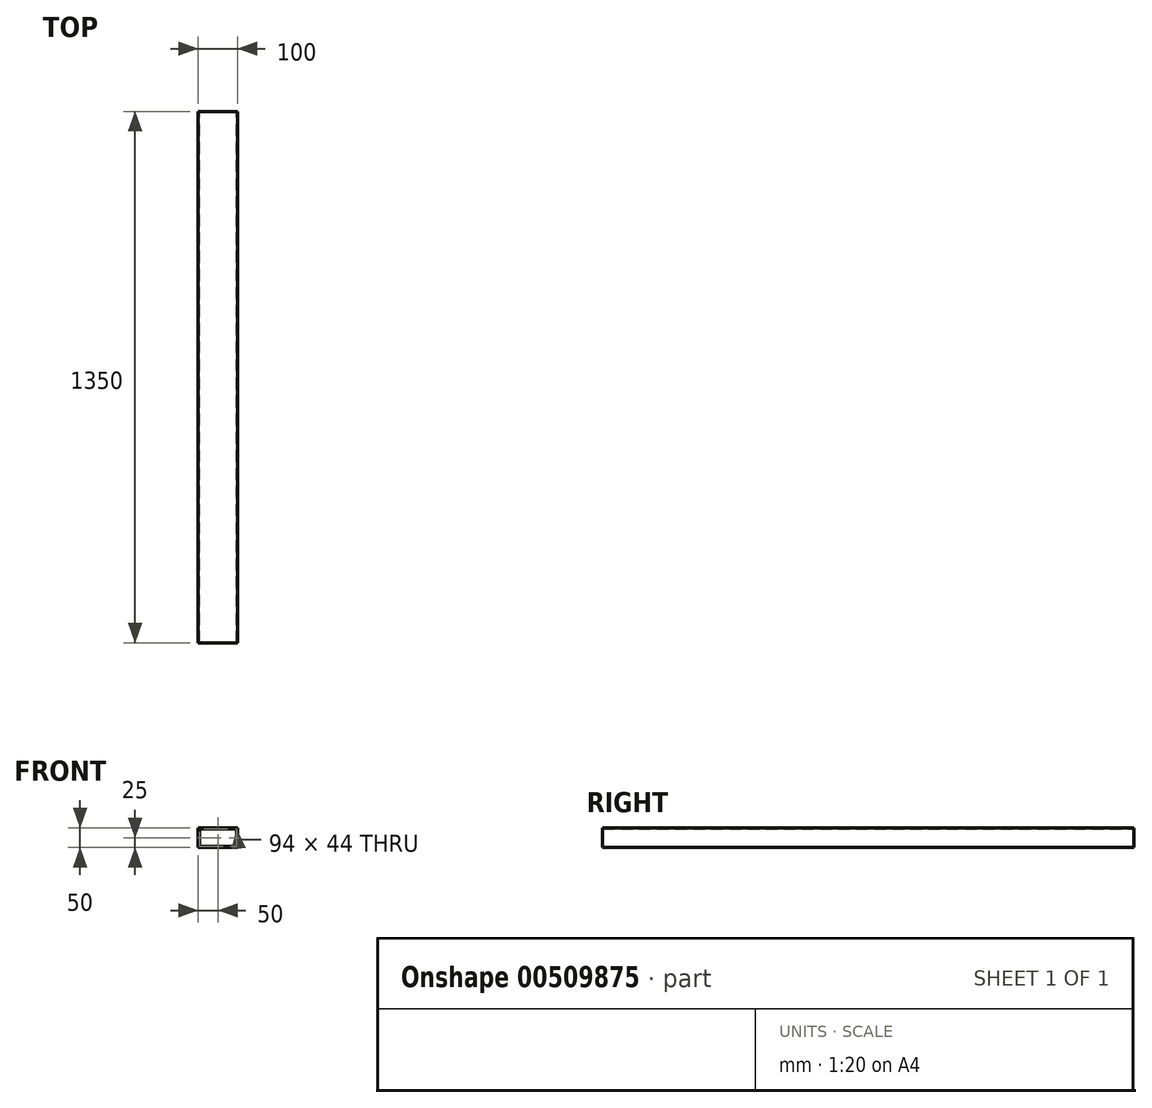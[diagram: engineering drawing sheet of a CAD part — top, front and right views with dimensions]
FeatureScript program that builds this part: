
annotation { "Feature Type Name" : "Feature", "Feature Type Description" : "" }
export const myFeature = defineFeature(function(context is Context, id is Id, definition is map)
    precondition{}
    {
        {
            var Q0;
            Q0=qCreatedBy(makeId("Front.planeOp"),FACE);
            var sketch = newSketch(context, id + "F0", { "sketchPlane" : qUnion([Q0])});
            skLineSegment(sketch, "E0.bottom", {"start": v(50, -25) * mm, "end": v(-50, -25) * mm});
            skLineSegment(sketch, "E0.top", {"start": v(50, 25) * mm, "end": v(-50, 25) * mm});
            skLineSegment(sketch, "E0.left", {"start": v(50, -25) * mm, "end": v(50, 25) * mm});
            skLineSegment(sketch, "E0.right", {"start": v(-50, -25) * mm, "end": v(-50, 25) * mm});
            skPoint(sketch, "E0.middle", {"position": v(0, 0) * mm});
            skLineSegment(sketch, "E1.bottom", {"start": v(47, -22) * mm, "end": v(-47, -22) * mm});
            skLineSegment(sketch, "E1.top", {"start": v(47, 22) * mm, "end": v(-47, 22) * mm});
            skLineSegment(sketch, "E1.left", {"start": v(47, -22) * mm, "end": v(47, 22) * mm});
            skLineSegment(sketch, "E1.right", {"start": v(-47, -22) * mm, "end": v(-47, 22) * mm});
            skSolve(sketch);
        }
        {
            var Q0;
            Q0=makeQuery(id+"F0.imprint","IMPRINT",FACE,{"disambiguationData":[TD([[makeQuery(id+"F0.imprint","IMPRINT",EDGE,{"derivedFrom":sQuery(id+"F0.wireOp",EDGE,"E0.bottom")}),-1.0]])]});
            extrude(context, id + "F1", {"entities" : qUnion([Q0]), "depth" : 1350 * mm, "offsetDistance" : 25 * mm});
        }
    });
